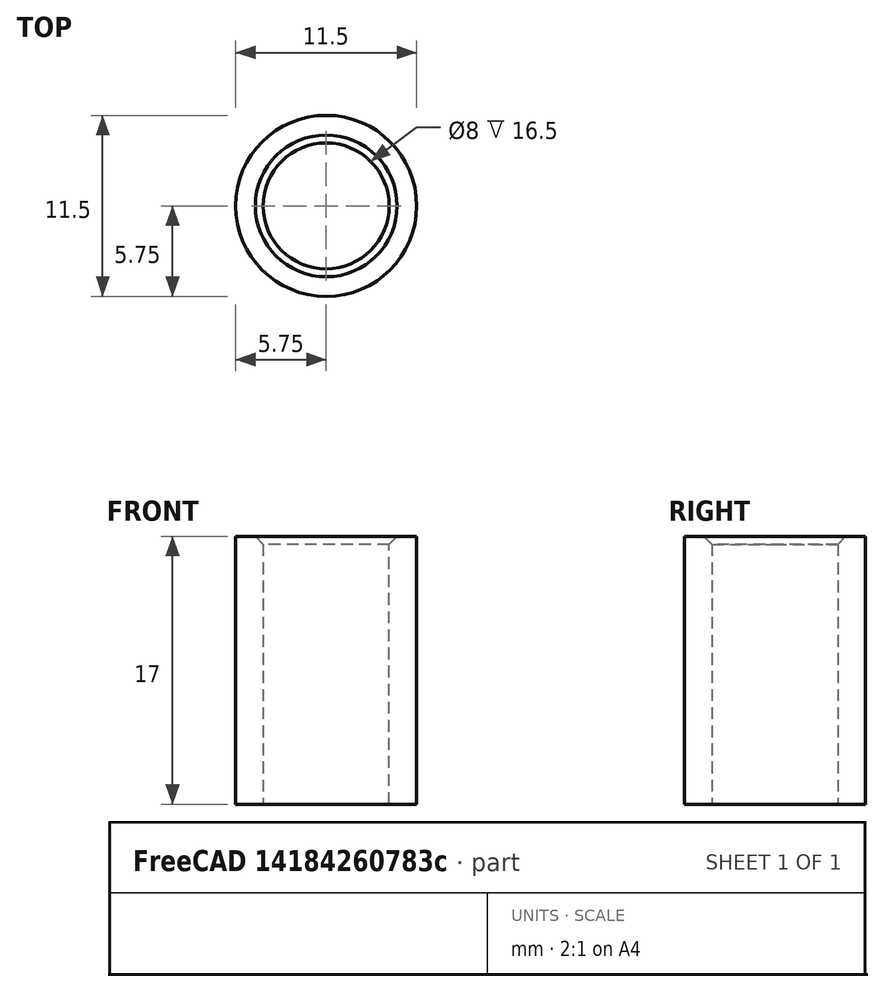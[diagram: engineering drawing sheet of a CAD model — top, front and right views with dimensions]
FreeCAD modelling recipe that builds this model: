
FCSTD DOCUMENT  (FreeCAD 0.19R24276 (Git))
Label: Ring_h17_5
License: All rights reserved
LicenseURL: http://en.wikipedia.org/wiki/All_rights_reserved
objects: Sketcher::SketchObject×1, PartDesign::Pad×1, PartDesign::Chamfer×1, PartDesign::Body×1
note: 6 computed .brp shape members not serialized (recipe doc carries the construction recipe); baked Part::Feature solids carry a one-line shape summary decoded from their .brp

FEATURE [Sketcher::SketchObject] Sketch
  FullyConstrained = true
  MapMode = 5
  Support = -> [XY_Plane]
  sketch-geometry (2):
    g0: Circle CenterX=0 CenterY=0 CenterZ=0 NormalX=0 NormalY=0 NormalZ=1 AngleXU=0 Radius=4
    g1: Circle CenterX=0 CenterY=0 CenterZ=0 NormalX=0 NormalY=0 NormalZ=1 AngleXU=0 Radius=5.75
  constraints (4):
    c: Coincident(g0,g-1)
    c: Coincident(g1,g0)
    c: Diameter(g0) = 8
    c: Diameter(g1) = 11.5
FEATURE [PartDesign::Pad] Pad
  Direction = (1,1,1)
  Length = 17
  Length2 = 100
  Profile = -> Sketch
  Type = 0
FEATURE [PartDesign::Chamfer] Chamfer
  Angle = 45
  Base = -> Pad [Edge6]
  BaseFeature = -> Pad
  ChamferType = 0
  FlipDirection = false
  Size = 0.5
  Size2 = 1
  SupportTransform = false
FEATURE [PartDesign::Body] Body
  Group = -> [Sketch,Pad,Chamfer]
  Origin = -> Origin
  Tip = -> Chamfer
